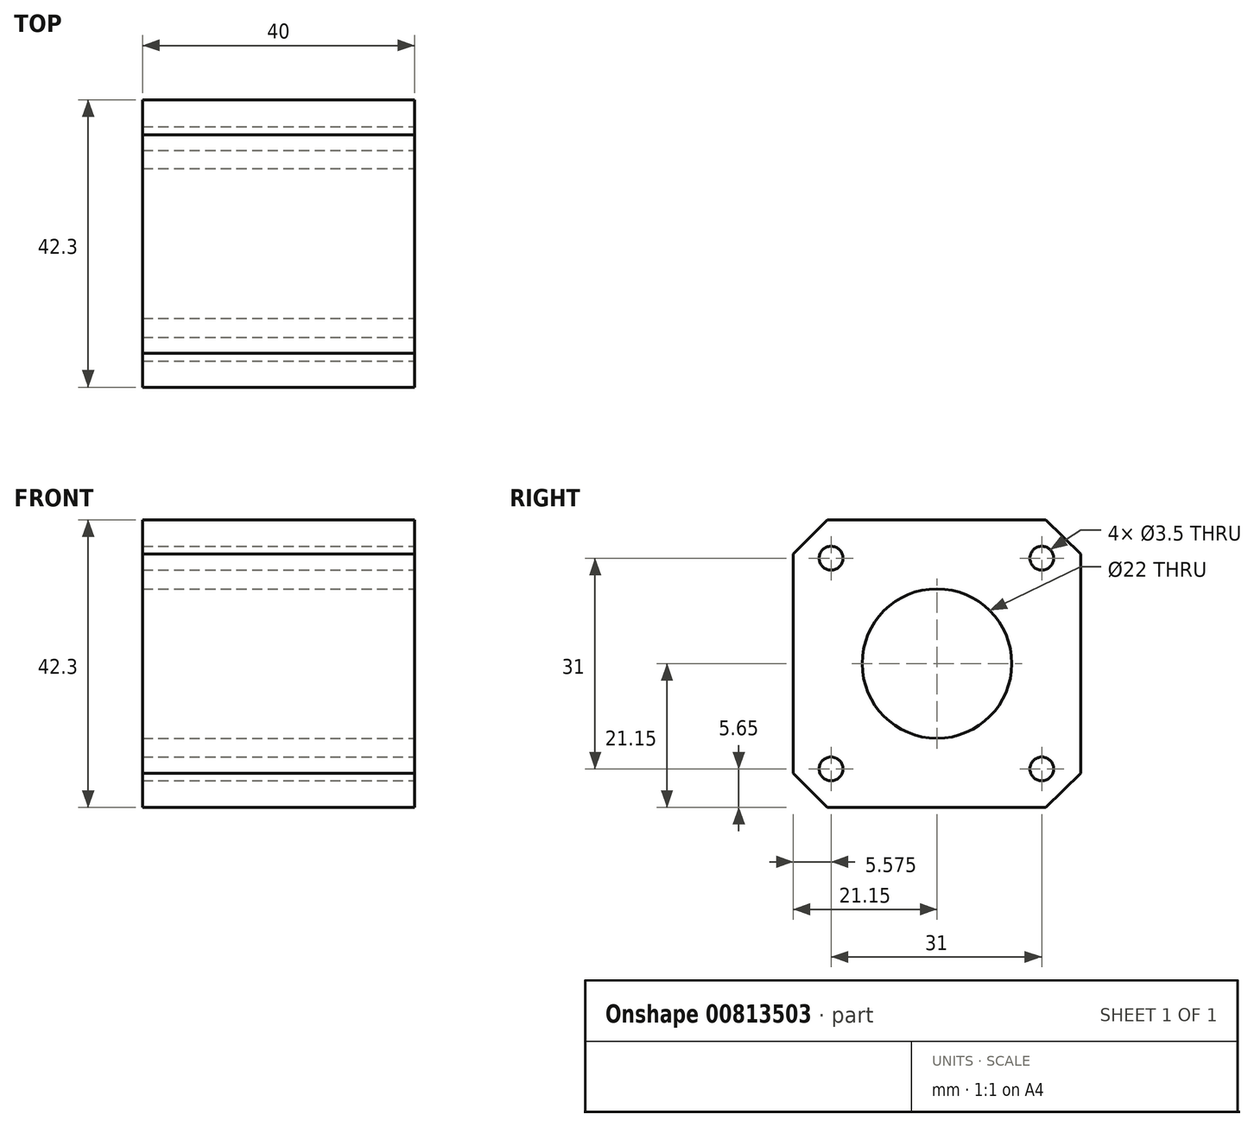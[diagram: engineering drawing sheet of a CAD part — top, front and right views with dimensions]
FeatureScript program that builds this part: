
annotation { "Feature Type Name" : "Feature", "Feature Type Description" : "" }
export const myFeature = defineFeature(function(context is Context, id is Id, definition is map)
    precondition{}
    {
        {
            var Q0;
            Q0=qCreatedBy(makeId("Right.planeOp"),FACE);
            var sketch = newSketch(context, id + "F0", { "sketchPlane" : qUnion([Q0])});
            skLineSegment(sketch, "E0.1", {"start": v(0, 0) * mm, "end": v(0, -42.3) * mm, "construction": true});
            skLineSegment(sketch, "E0.2", {"start": v(0, -21.15) * mm, "end": v(-25.15, -21.15) * mm, "construction": true});
            skCircle(sketch, "E0.3", {"center": v(-25.15, -21.15) * mm, "radius": 11 * mm});
            skLineSegment(sketch, "E0.4", {"start": v(-9.73, -36.65) * mm, "end": v(-9.73, -5.65) * mm, "construction": true});
            skLineSegment(sketch, "E0.6", {"start": v(-40.73, -36.65) * mm, "end": v(-40.73, -5.65) * mm, "construction": true});
            skLineSegment(sketch, "E0.7", {"start": v(-9.73, -36.65) * mm, "end": v(-40.73, -36.65) * mm, "construction": true});
            skLineSegment(sketch, "E0.8", {"start": v(-9.73, -5.65) * mm, "end": v(-40.73, -5.65) * mm, "construction": true});
            skCircle(sketch, "E0.9", {"center": v(-40.73, -5.65) * mm, "radius": 1.75 * mm});
            skCircle(sketch, "E0.10", {"center": v(-40.73, -36.65) * mm, "radius": 1.75 * mm});
            skCircle(sketch, "E0.11", {"center": v(-9.73, -36.65) * mm, "radius": 1.75 * mm});
            skCircle(sketch, "E0.12", {"center": v(-9.73, -5.65) * mm, "radius": 1.75 * mm});
            skLineSegment(sketch, "E1.0.0", {"start": v(-41.3, -42.3) * mm, "end": v(-9.15, -42.3) * mm});
            skLineSegment(sketch, "E1.0.1", {"start": v(-41.3, -42.3) * mm, "end": v(-46.3, -37.3) * mm});
            skLineSegment(sketch, "E1.0.2", {"start": v(-46.3, -5) * mm, "end": v(-46.3, -37.3) * mm});
            skLineSegment(sketch, "E1.0.3", {"start": v(-46.3, -5) * mm, "end": v(-41.3, 0) * mm});
            skLineSegment(sketch, "E1.0.4", {"start": v(-41.3, 0) * mm, "end": v(-9.15, 0) * mm});
            skLineSegment(sketch, "E1.0.5", {"start": v(-4, -5) * mm, "end": v(-4, -37.3) * mm});
            skLineSegment(sketch, "E2", {"start": v(-25.15, 0) * mm, "end": v(-25.15, -42.3) * mm, "construction": true});
            skLineSegment(sketch, "E3.MirrorCS", {"start": v(-9.15, -42.3) * mm, "end": v(-4, -37.3) * mm});
            skLineSegment(sketch, "E4.MirrorCS", {"start": v(-9.15, 0) * mm, "end": v(-4, -5) * mm});
            skSolve(sketch);
        }
        {
            var Q0;
            Q0=qSketchRegion(id+"F0",true);
            extrude(context, id + "F1", {"entities" : qUnion([Q0]), "oppositeDirection" : true, "depth" : 40 * mm, "offsetDistance" : 25 * mm});
        }
    });
